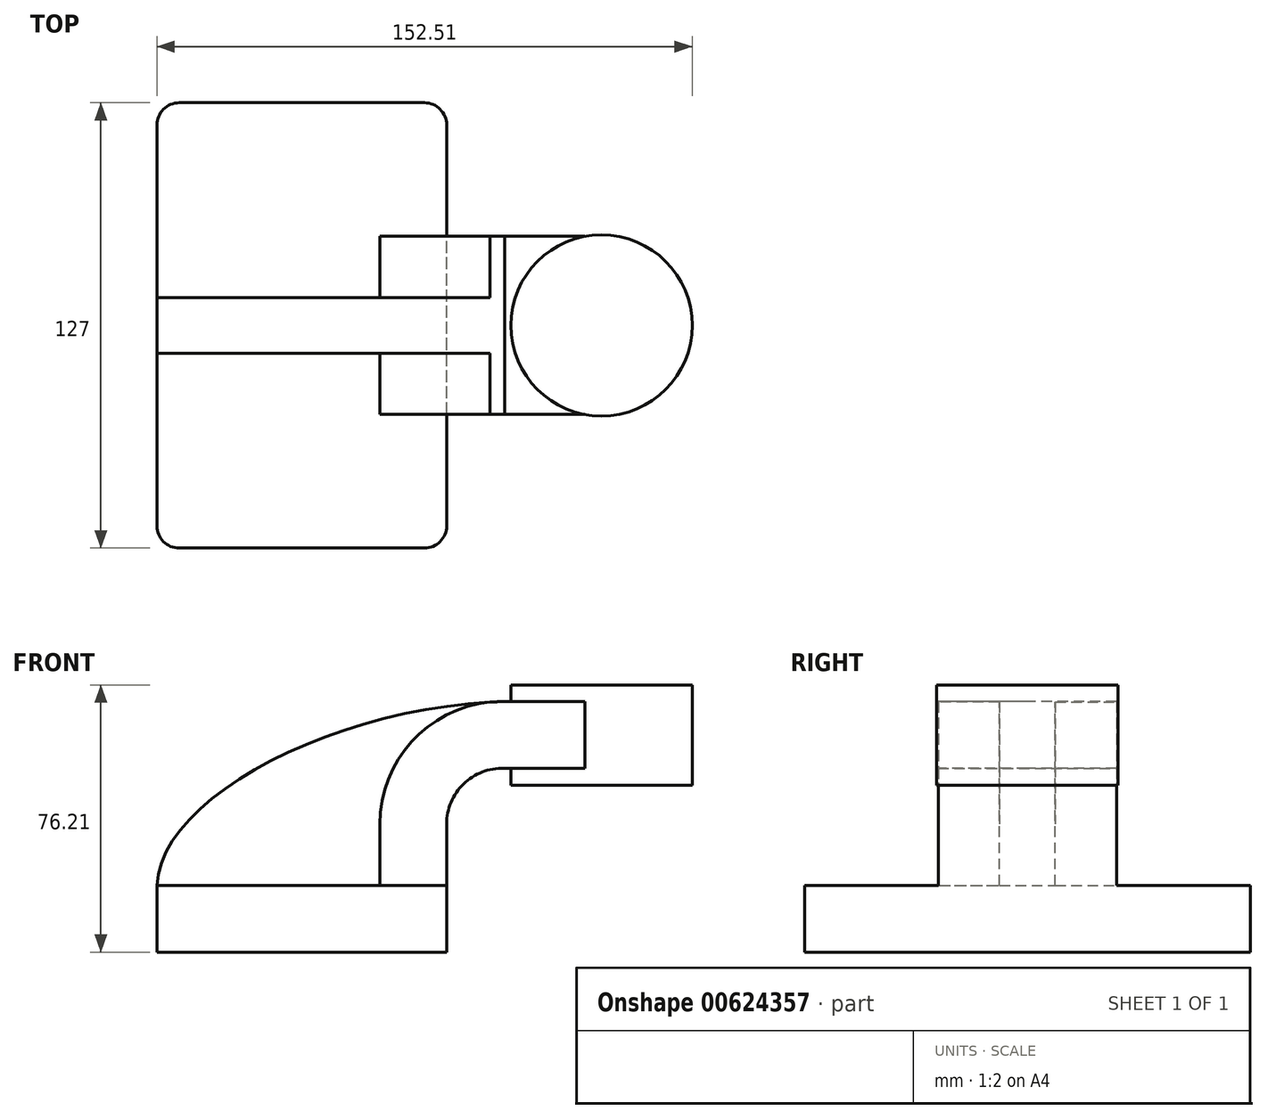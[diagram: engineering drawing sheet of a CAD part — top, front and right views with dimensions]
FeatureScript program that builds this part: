
annotation { "Feature Type Name" : "Feature", "Feature Type Description" : "" }
export const myFeature = defineFeature(function(context is Context, id is Id, definition is map)
    precondition{}
    {
        {
            var Q0;
            Q0=qCreatedBy(makeId("Front.planeOp"),FACE);
            var sketch = newSketch(context, id + "F0", { "sketchPlane" : qUnion([Q0])});
            skLineSegment(sketch, "E0.bottom", {"start": v(41.28, -9.52) * mm, "end": v(-41.28, -9.53) * mm});
            skLineSegment(sketch, "E0.top", {"start": v(41.28, 9.53) * mm, "end": v(-41.28, 9.53) * mm});
            skLineSegment(sketch, "E0.left", {"start": v(41.28, -9.52) * mm, "end": v(41.28, 9.53) * mm});
            skLineSegment(sketch, "E0.right", {"start": v(-41.28, -9.53) * mm, "end": v(-41.28, 9.53) * mm});
            skPoint(sketch, "E0.middle", {"position": v(0, 0) * mm});
            skLineSegment(sketch, "E1.bottom", {"start": v(111.23, 38.1) * mm, "end": v(60.43, 38.1) * mm});
            skLineSegment(sketch, "E1.top", {"start": v(111.23, 66.68) * mm, "end": v(60.43, 66.68) * mm});
            skLineSegment(sketch, "E1.left", {"start": v(111.23, 38.1) * mm, "end": v(111.23, 66.68) * mm});
            skLineSegment(sketch, "E1.right", {"start": v(60.43, 38.1) * mm, "end": v(60.43, 66.68) * mm});
            skPoint(sketch, "E1.middle", {"position": v(85.83, 52.39) * mm});
            skLineSegment(sketch, "E2", {"start": v(41.28, 9.53) * mm, "end": v(41.28, 27) * mm});
            skArc(sketch, "E3", {"start": v(41.27, 27) * mm, "mid": v(46.1, 38.4) * mm, "end": v(57.62, 42.88) * mm});
            skLineSegment(sketch, "E4", {"start": v(57.62, 42.88) * mm, "end": v(85.4, 42.88) * mm});
            skLineSegment(sketch, "E5.0", {"start": v(57.85, 61.93) * mm, "end": v(85.4, 61.93) * mm});
            skArc(sketch, "E5.1", {"start": v(22.23, 27) * mm, "mid": v(32.7, 51.95) * mm, "end": v(57.85, 61.93) * mm});
            skLineSegment(sketch, "E5.2", {"start": v(22.22, 9.53) * mm, "end": v(22.22, 27) * mm});
            skLineSegment(sketch, "E6", {"start": v(85.4, 42.88) * mm, "end": v(85.4, 61.93) * mm});
            skFitSpline(sketch, "E7", {"points": [v(-41.28, 9.53) * mm, v(57.85, 61.93) * mm], "startDerivative": vector(2.6, 74.66) * mm, "endDerivative": vector(145.72, 3.72) * mm});
            skLineSegment(sketch, "E8", {"start": v(85.4, 38.1) * mm, "end": v(85.4, 66.68) * mm});
            skPoint(sketch, "E8.startSnap0", {"position": v(85.83, 38.1) * mm});
            skSolve(sketch);
        }
        {
            var Q0;
            Q0=makeQuery(id+"F0.imprint","IMPRINT",FACE,{"disambiguationData":[TD([[makeQuery(id+"F0.imprint","IMPRINT",EDGE,{"derivedFrom":sQuery(id+"F0.wireOp",EDGE,"E0.bottom")}),-1.0]])]});
            extrude(context, id + "F1", {"entities" : qUnion([Q0]), "endBound" : BoundingType.SYMMETRIC, "depth" : 127 * mm, "offsetDistance" : 25.4 * mm});
        }
        {
            var Q0;
            {var subQ1=sQuery(id+"F0.wireOp",EDGE,"E2");Q0=makeQuery(id+"F0.imprint","IMPRINT",FACE,{"disambiguationData":[TD([[makeQuery(id+"F0.imprint","IMPRINT",EDGE,{"derivedFrom":subQ1}),1.0]])]});}
            var Q1;
            {var subQ0=sQuery(id+"F0.wireOp",EDGE,"E4");var subQ1=sQuery(id+"F0.wireOp",EDGE,"E1.right");var subQ2=makeQuery(id+"F0.imprint","INTERSECT",VERTEX,{"derivedFrom":[subQ1,subQ0]});Q1=makeQuery(id+"F0.imprint","IMPRINT",FACE,{"disambiguationData":[TD([[makeQuery(id+"F0.imprint","IMPRINT",EDGE,{"disambiguationData":[TD([[subQ2,-1.0]])],"derivedFrom":subQ1}),-1.0]])]});}
            extrude(context, id + "F2", {"entities" : qUnion([Q0, Q1]), "operationType" : NewBodyOperationType.ADD, "endBound" : BoundingType.SYMMETRIC, "depth" : 50.8 * mm, "offsetDistance" : 25.4 * mm});
        }
        {
            var Q0;
            {var subQ3=sQuery(id+"F0.wireOp",EDGE,"E5.2");Q0=makeQuery(id+"F0.imprint","IMPRINT",FACE,{"disambiguationData":[TD([[makeQuery(id+"F0.imprint","IMPRINT",EDGE,{"derivedFrom":subQ3}),1.0]])]});}
            extrude(context, id + "F3", {"entities" : qUnion([Q0]), "operationType" : NewBodyOperationType.ADD, "endBound" : BoundingType.SYMMETRIC, "depth" : 15.88 * mm, "offsetDistance" : 25.4 * mm});
        }
        {
            var Q0;
            {var subQ4=sQuery(id+"F0.wireOp",EDGE,"E1.left");Q0=makeQuery(id+"F0.imprint","IMPRINT",FACE,{"disambiguationData":[TD([[makeQuery(id+"F0.imprint","IMPRINT",EDGE,{"derivedFrom":subQ4}),1.0]])]});}
            var Q1;
            Q1=sQuery(id+"F0.wireOp",EDGE,"E8");
            revolve(context, id + "F4", {"operationType" : NewBodyOperationType.ADD, "entities" : qUnion([Q0]), "axis" : qUnion([Q1]), "revolveType" : RevolveType.FULL});
        }
        {
            var Q0;
            Q0=makeQuery(id+"F1.opExtrude","CAP_EDGE",EDGE,{"disambiguationData":[OSD([sQuery(id+"F0.wireOp",EDGE,"E0.left")])],"isStart":false});
            var Q1;
            Q1=makeQuery(id+"F1.opExtrude","CAP_EDGE",EDGE,{"disambiguationData":[OSD([sQuery(id+"F0.wireOp",EDGE,"E0.right")])],"isStart":false});
            var Q2;
            Q2=makeQuery(id+"F1.opExtrude","CAP_EDGE",EDGE,{"disambiguationData":[OSD([sQuery(id+"F0.wireOp",EDGE,"E0.right")])],"isStart":true});
            var Q3;
            Q3=makeQuery(id+"F1.opExtrude","CAP_EDGE",EDGE,{"disambiguationData":[OSD([sQuery(id+"F0.wireOp",EDGE,"E0.left")])],"isStart":true});
            fillet(context, id + "F5", {"entities" : qUnion([Q0, Q1, Q2, Q3]), "radius" : 6.35 * mm, "tangentPropagation" : true, "allowEdgeOverflow" : false});
        }
    });
